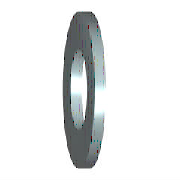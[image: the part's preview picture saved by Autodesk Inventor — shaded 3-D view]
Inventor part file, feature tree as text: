
AUTODESK INVENTOR PART (.ipt)
format: ipt  version: 2022.1 (Build 261234000, 234)  size: 108,032 bytes
history: native  units: mm (DEFAULTED — no unit token found)
features: extrude x1, other x1, plane x1, sketch x1
ambient origin geometry x7: Origin, YZ Plane, XY Plane, X Axis, Y Axis, Z Axis, Center Point
bodies: Solid1 (feature_tree)
feature tree (4):
  extrude  "Cuerpo"  Depth=1.6mm
  other  "Work Axis1"
  plane  "Work Plane1"
  sketch  "Boceto"  dims[d0=8.4mm d1=16.0mm d2=1.6mm d3=0.0mm d4=0.0mm d5=0.0mm d6=0.0mm d7=0.0mm]
